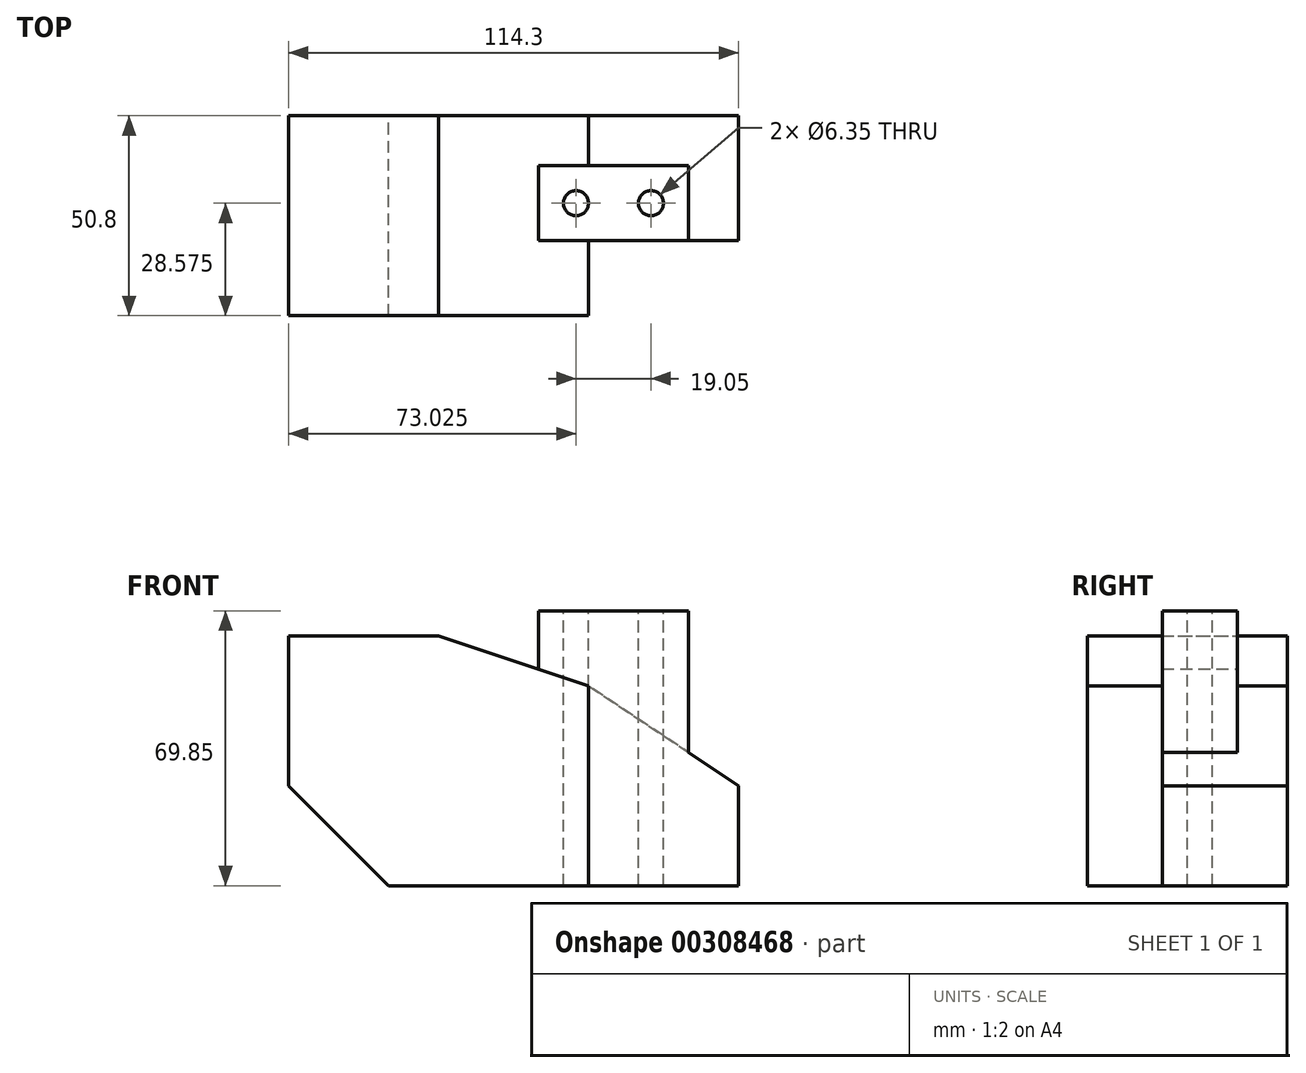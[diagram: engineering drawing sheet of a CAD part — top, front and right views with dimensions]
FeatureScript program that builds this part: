
annotation { "Feature Type Name" : "Feature", "Feature Type Description" : "" }
export const myFeature = defineFeature(function(context is Context, id is Id, definition is map)
    precondition{}
    {
        {
            var Q0;
            Q0=qCreatedBy(makeId("Front.planeOp"),FACE);
            var sketch = newSketch(context, id + "F0", { "sketchPlane" : qUnion([Q0])});
            skLineSegment(sketch, "E0", {"start": v(0, 0) * mm, "end": v(50.8, 0) * mm});
            skLineSegment(sketch, "E1", {"start": v(50.8, 0) * mm, "end": v(50.8, 50.8) * mm});
            skLineSegment(sketch, "E2", {"start": v(50.8, 50.8) * mm, "end": v(12.7, 63.5) * mm});
            skLineSegment(sketch, "E3", {"start": v(12.7, 63.5) * mm, "end": v(-25.4, 63.5) * mm});
            skLineSegment(sketch, "E4", {"start": v(-25.4, 63.5) * mm, "end": v(-25.4, 25.4) * mm});
            skLineSegment(sketch, "E5", {"start": v(-25.4, 25.4) * mm, "end": v(0, 0) * mm});
            skSolve(sketch);
        }
        {
            var Q0;
            Q0=makeQuery(id+"F0.imprint","IMPRINT",FACE,{"disambiguationData":[TD([[makeQuery(id+"F0.imprint","IMPRINT",EDGE,{"derivedFrom":sQuery(id+"F0.wireOp",EDGE,"E0")}),1.0]])]});
            extrude(context, id + "F1", {"entities" : qUnion([Q0]), "depth" : 50.8 * mm});
        }
        {
            var Q0;
            Q0=makeQuery(id+"F1.opExtrude","CAP_FACE",FACE,{"disambiguationData":[OSD([sQuery(id+"F0.wireOp",EDGE,"E0"),sQuery(id+"F0.wireOp",EDGE,"E1"),sQuery(id+"F0.wireOp",EDGE,"E2"),sQuery(id+"F0.wireOp",EDGE,"E3"),sQuery(id+"F0.wireOp",EDGE,"E4"),sQuery(id+"F0.wireOp",EDGE,"E5")])],"isStart":true});
            var sketch = newSketch(context, id + "F2", { "sketchPlane" : qUnion([Q0])});
            skLineSegment(sketch, "E6", {"start": v(-50.8, 0) * mm, "end": v(-88.9, 0) * mm});
            skLineSegment(sketch, "E7", {"start": v(-88.9, 0) * mm, "end": v(-88.9, 25.4) * mm});
            skLineSegment(sketch, "E8", {"start": v(-88.9, 25.4) * mm, "end": v(-50.8, 50.8) * mm});
            skSolve(sketch);
        }
        {
            var Q0;
            Q0=makeQuery(id+"F2.imprint","IMPRINT",FACE,{"disambiguationData":[TD([[makeQuery(id+"F2.imprint","IMPRINT",EDGE,{"derivedFrom":sQuery(id+"F2.wireOp",EDGE,"E6")}),-1.0]])]});
            extrude(context, id + "F3", {"entities" : qUnion([Q0]), "operationType" : NewBodyOperationType.ADD, "oppositeDirection" : true, "depth" : 31.75 * mm});
        }
        {
            var Q0;
            Q0=makeQuery(id+"F3.boolean.opBoolean","MERGE",FACE,{"derivedFrom":[makeQuery(id+"F1.opExtrude","SWEPT_FACE",FACE,{"disambiguationData":[OSD([sQuery(id+"F0.wireOp",EDGE,"E0")])]}),makeQuery(id+"F3.opExtrude","SWEPT_FACE",FACE,{"disambiguationData":[OSD([sQuery(id+"F2.wireOp",EDGE,"E6")])]})]});
            var sketch = newSketch(context, id + "F4", { "sketchPlane" : qUnion([Q0])});
            skLineSegment(sketch, "E9", {"start": v(76.2, 31.75) * mm, "end": v(38.1, 31.75) * mm});
            skLineSegment(sketch, "E10", {"start": v(38.1, 31.75) * mm, "end": v(38.1, 12.7) * mm});
            skLineSegment(sketch, "E11", {"start": v(38.1, 12.7) * mm, "end": v(76.2, 12.7) * mm});
            skLineSegment(sketch, "E12", {"start": v(76.2, 12.7) * mm, "end": v(76.2, 31.75) * mm});
            skSolve(sketch);
        }
        {
            var Q0;
            {var subQ0=sQuery(id+"F4.wireOp",EDGE,"E10");Q0=makeQuery(id+"F4.imprint","IMPRINT",FACE,{"disambiguationData":[TD([[makeQuery(id+"F4.imprint","IMPRINT",EDGE,{"derivedFrom":subQ0}),1.0]])]});}
            extrude(context, id + "F5", {"entities" : qUnion([Q0]), "operationType" : NewBodyOperationType.ADD, "oppositeDirection" : true, "depth" : 69.85 * mm});
        }
        {
            var Q0;
            Q0=makeQuery(id+"F5.opExtrude","CAP_FACE",FACE,{"disambiguationData":[OSD([sQuery(id+"F4.wireOp",EDGE,"E9"),sQuery(id+"F4.wireOp",EDGE,"E10"),sQuery(id+"F4.wireOp",EDGE,"E11"),sQuery(id+"F4.wireOp",EDGE,"E12")])],"isStart":false});
            var sketch = newSketch(context, id + "F6", { "sketchPlane" : qUnion([Q0])});
            skCircle(sketch, "E13", {"center": v(47.62, -22.23) * mm, "radius": 3.18 * mm});
            skCircle(sketch, "E14", {"center": v(66.67, -22.23) * mm, "radius": 3.18 * mm});
            skSolve(sketch);
        }
        {
            var Q0;
            Q0 = qSketchRegion(id + "F6", true);
            extrude(context, id + "F7", {"entities" : qUnion([Q0]), "operationType" : NewBodyOperationType.REMOVE, "endBound" : BoundingType.THROUGH_ALL, "oppositeDirection" : true, "depth" : 25.4 * mm});
        }
    });
